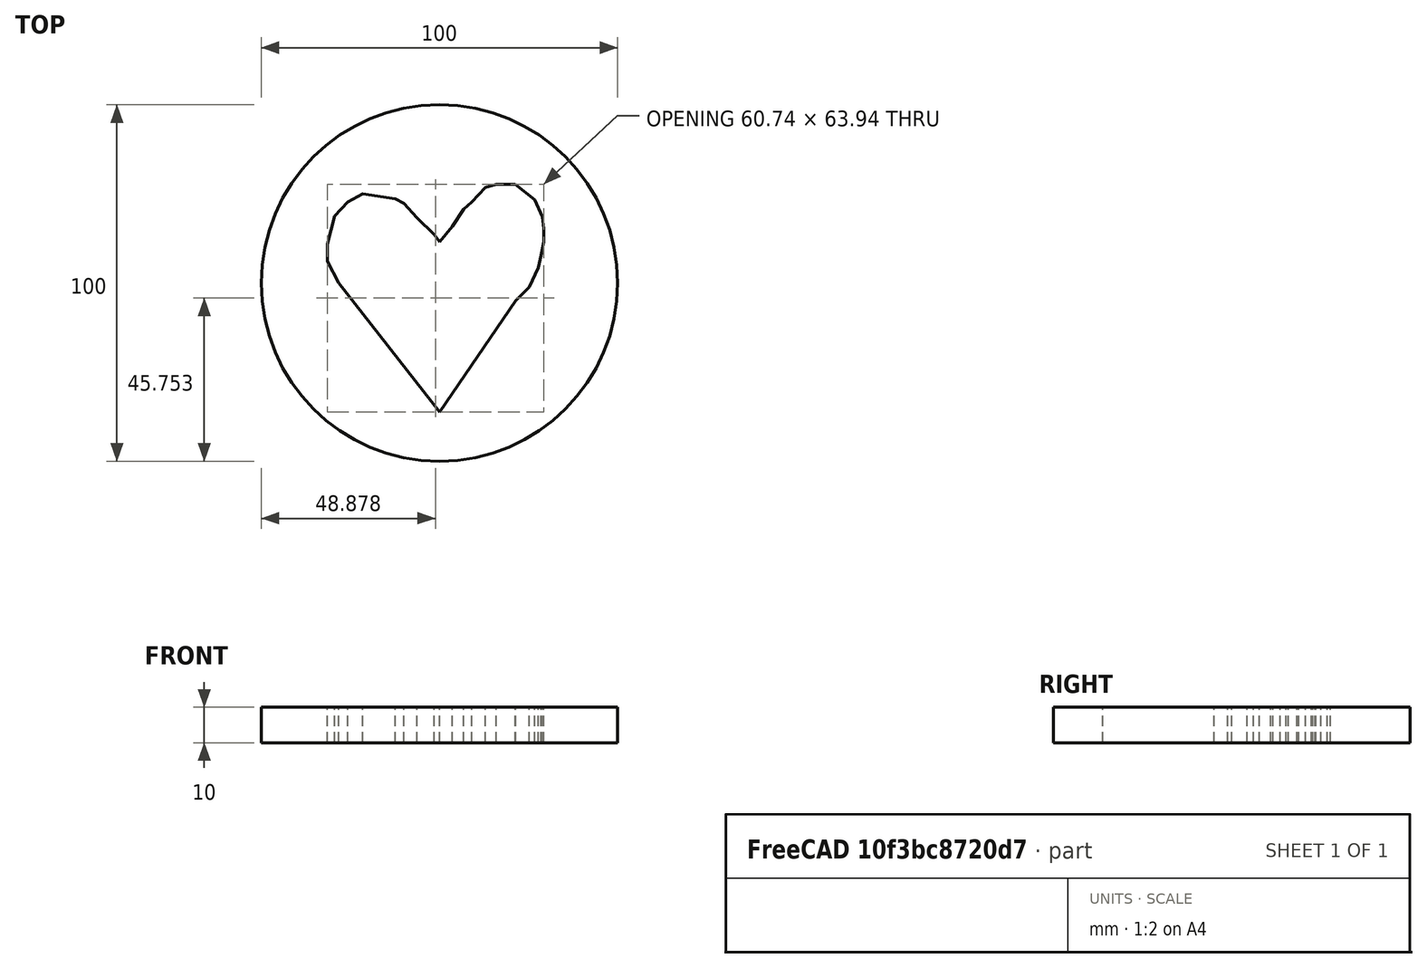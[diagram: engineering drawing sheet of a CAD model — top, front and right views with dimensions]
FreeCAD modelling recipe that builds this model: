
FCSTD DOCUMENT  (FreeCAD 0.20R29177 +233 (Git))
Label: corazon
License: All rights reserved
LicenseURL: http://en.wikipedia.org/wiki/All_rights_reserved
objects: Sketcher::SketchObject×1, Part::Extrusion×1
note: 2 computed .brp shape members not serialized (recipe doc carries the construction recipe); baked Part::Feature solids carry a one-line shape summary decoded from their .brp

FEATURE [Sketcher::SketchObject] Sketch
  FullyConstrained = false
  sketch-geometry (27):
    g0: Circle CenterX=0 CenterY=0 CenterZ=0 NormalX=0 NormalY=0 NormalZ=1 AngleXU=0 Radius=50
    g1: LineSegment StartX=0 StartY=-36.2179 StartZ=0 EndX=-28.2853 EndY=0 EndZ=0
    g2: LineSegment StartX=-28.2853 StartY=0 StartZ=0 EndX=-31.4904 EndY=6.08974 EndZ=0
    g3: LineSegment StartX=-31.4904 StartY=6.08974 StartZ=0 EndX=-31.4904 EndY=10.8974 EndZ=0
    g4: LineSegment StartX=-31.4904 StartY=10.8974 StartZ=0 EndX=-29.4071 EndY=18.75 EndZ=0
    g5: LineSegment StartX=-29.4071 StartY=18.75 StartZ=0 EndX=-25.7211 EndY=22.7564 EndZ=0
    g6: LineSegment StartX=-25.7211 StartY=22.7564 StartZ=0 EndX=-21.5545 EndY=25 EndZ=0
    g7: LineSegment StartX=-21.5545 StartY=25 StartZ=0 EndX=-12.4199 EndY=23.5577 EndZ=0
    g8: LineSegment StartX=-12.4199 StartY=23.5577 StartZ=0 EndX=-10.016 EndY=22.2756 EndZ=0
    g9: LineSegment StartX=-10.016 StartY=22.2756 StartZ=0 EndX=-6.33012 EndY=18.2692 EndZ=0
    g10: LineSegment StartX=-6.33012 StartY=18.2692 StartZ=0 EndX=-1.52243 EndY=13.6218 EndZ=0
    g11: LineSegment StartX=-1.52243 StartY=13.6218 StartZ=0 EndX=0 EndY=11.5385 EndZ=0
    g12: LineSegment StartX=0 StartY=11.5385 StartZ=0 EndX=3.60577 EndY=15.8654 EndZ=0
    g13: LineSegment StartX=3.60577 StartY=15.8654 StartZ=0 EndX=6.81091 EndY=20.6731 EndZ=0
    g14: LineSegment StartX=6.81091 StartY=20.6731 StartZ=0 EndX=9.05449 EndY=22.7564 EndZ=0
    g15: LineSegment StartX=9.05449 StartY=22.7564 StartZ=0 EndX=12.9006 EndY=26.7628 EndZ=0
    g16: LineSegment StartX=12.9006 StartY=26.7628 StartZ=0 EndX=15.9455 EndY=27.7244 EndZ=0
    g17: LineSegment StartX=15.9455 StartY=27.7244 StartZ=0 EndX=21.234 EndY=27.7244 EndZ=0
    g18: LineSegment StartX=21.234 StartY=27.7244 StartZ=0 EndX=26.6827 EndY=23.3974 EndZ=0
    g19: LineSegment StartX=26.6827 StartY=23.3974 StartZ=0 EndX=28.9263 EndY=18.5897 EndZ=0
    g20: LineSegment StartX=28.9263 StartY=18.5897 StartZ=0 EndX=29.2468 EndY=15.2244 EndZ=0
    g21: LineSegment StartX=29.2468 StartY=15.2244 StartZ=0 EndX=29.2468 EndY=11.5385 EndZ=0
    g22: LineSegment StartX=29.2468 StartY=11.5385 StartZ=0 EndX=28.4455 EndY=7.69231 EndZ=0
    g23: LineSegment StartX=28.4455 StartY=7.69231 StartZ=0 EndX=27.8045 EndY=4.32692 EndZ=0
    g24: LineSegment StartX=27.8045 StartY=4.32692 StartZ=0 EndX=25.2404 EndY=-1.12179 EndZ=0
    g25: LineSegment StartX=25.2404 StartY=-1.12179 StartZ=0 EndX=21.3942 EndY=-4.96795 EndZ=0
    g26: LineSegment StartX=21.3942 StartY=-4.96795 StartZ=0 EndX=0 EndY=-36.2179 EndZ=0
  constraints (34):
    c: Coincident(g0,g-1)
    c: PointOnObject(g1,g-2)
    c: PointOnObject(g1,g-1)
    c: Coincident(g1,g2)
    c: Coincident(g2,g3)
    c: Vertical(g3)
    c: Coincident(g3,g4)
    c: Coincident(g4,g5)
    c: Coincident(g5,g6)
    c: Coincident(g6,g7)
    c: Coincident(g7,g8)
    c: Coincident(g8,g9)
    c: Coincident(g9,g10)
    c: Coincident(g10,g11)
    c: PointOnObject(g11,g-2)
    c: Coincident(g11,g12)
    c: Coincident(g12,g13)
    c: Coincident(g13,g14)
    c: Coincident(g14,g15)
    c: Coincident(g15,g16)
    c: Coincident(g16,g17)
    c: Horizontal(g17)
    c: Coincident(g17,g18)
    c: Coincident(g18,g19)
    c: Coincident(g19,g20)
    c: Coincident(g20,g21)
    c: Vertical(g21)
    c: Coincident(g21,g22)
    c: Coincident(g22,g23)
    c: Coincident(g23,g24)
    c: Coincident(g24,g25)
    c: Coincident(g25,g26)
    c: Coincident(g26,g1)
    c: Diameter(g0) = 100
FEATURE [Part::Extrusion] Extrude
  Base = -> Sketch
  Dir = (0,0,1)
  DirMode = 2
  FaceMakerClass = Part::FaceMakerBullseye
  LengthFwd = 10
  LengthRev = 0
  Solid = true
  Symmetric = false
